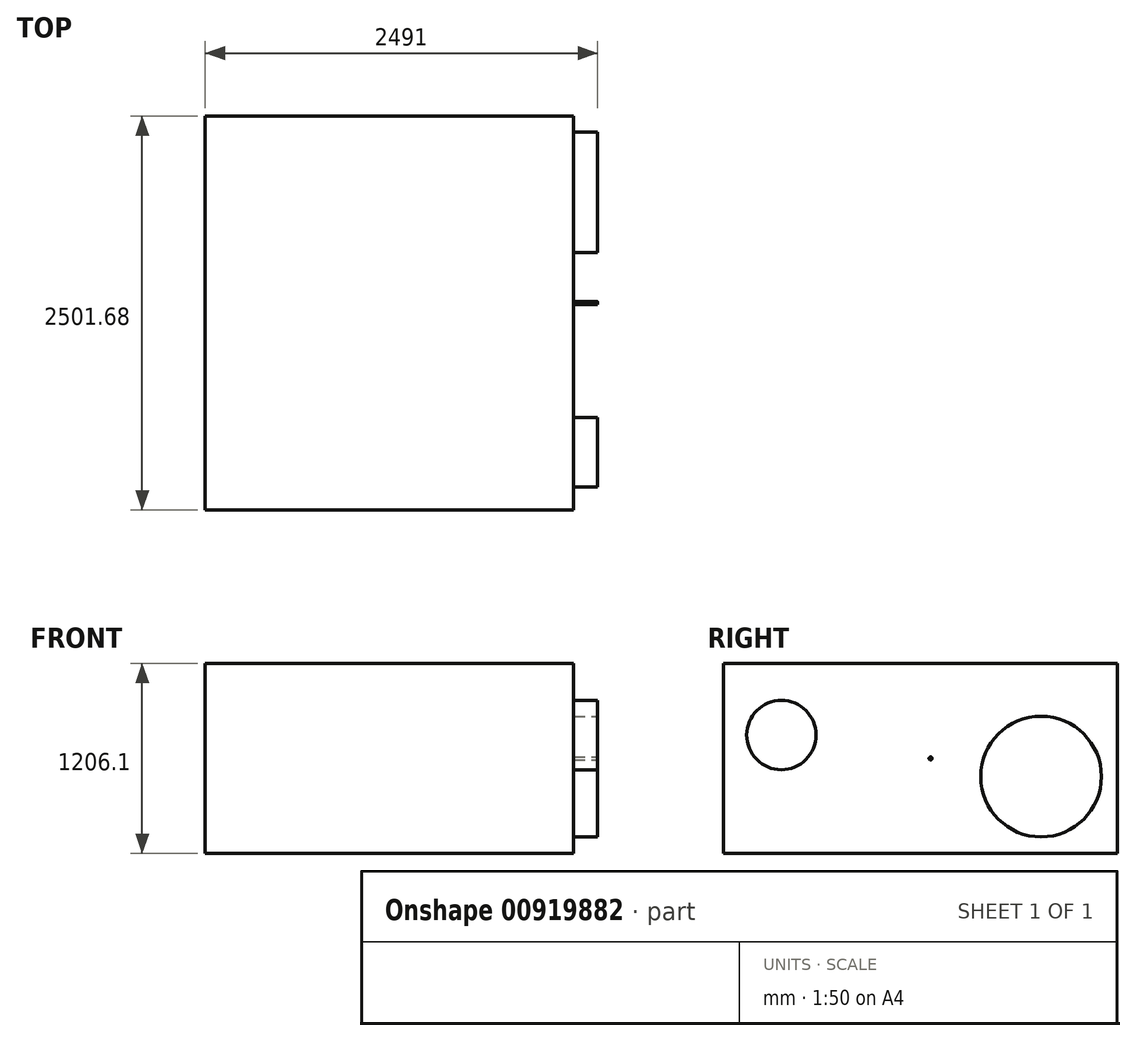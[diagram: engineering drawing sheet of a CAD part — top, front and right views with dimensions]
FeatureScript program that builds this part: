
annotation { "Feature Type Name" : "Feature", "Feature Type Description" : "" }
export const myFeature = defineFeature(function(context is Context, id is Id, definition is map)
    precondition{}
    {
        {
            var Q0;
            Q0=qCreatedBy(makeId("Right.planeOp"),FACE);
            var sketch = newSketch(context, id + "F0", { "sketchPlane" : qUnion([Q0])});
            skCircle(sketch, "E0", {"center": v(64.6, 0) * mm, "radius": 9.65 * mm});
            skCircle(sketch, "E1", {"center": v(766.5, -115.28) * mm, "radius": 383.18 * mm});
            skCircle(sketch, "E2", {"center": v(-883.14, 148.14) * mm, "radius": 220.27 * mm});
            skSolve(sketch);
        }
        {
            var Q0;
            Q0 = qSketchRegion(id + "F0", true);
            extrude(context, id + "F1", {"entities" : qUnion([Q0]), "oppositeDirection" : true, "depth" : 153.94 * mm, "offsetDistance" : 25.4 * mm});
        }
        {
            var Q0;
            Q0=makeQuery(id+"F1.opExtrude","CAP_FACE",FACE,{"disambiguationData":[OSD([sQuery(id+"F0.wireOp",EDGE,"E2")])],"isStart":false});
            var sketch = newSketch(context, id + "F2", { "sketchPlane" : qUnion([Q0])});
            skLineSegment(sketch, "E3.bottom", {"start": v(-1250.84, -603.05) * mm, "end": v(1250.84, -603.05) * mm});
            skLineSegment(sketch, "E3.top", {"start": v(-1250.84, 603.05) * mm, "end": v(1250.84, 603.05) * mm});
            skLineSegment(sketch, "E3.left", {"start": v(-1250.84, -603.05) * mm, "end": v(-1250.84, 603.05) * mm});
            skLineSegment(sketch, "E3.right", {"start": v(1250.84, -603.05) * mm, "end": v(1250.84, 603.05) * mm});
            skPoint(sketch, "E3.middle", {"position": v(0, 0) * mm});
            skSolve(sketch);
        }
        {
            var Q0;
            Q0 = qSketchRegion(id + "F2", true);
            extrude(context, id + "F3", {"entities" : qUnion([Q0]), "depth" : 2337.07 * mm, "offsetDistance" : 25.4 * mm});
        }
    });
